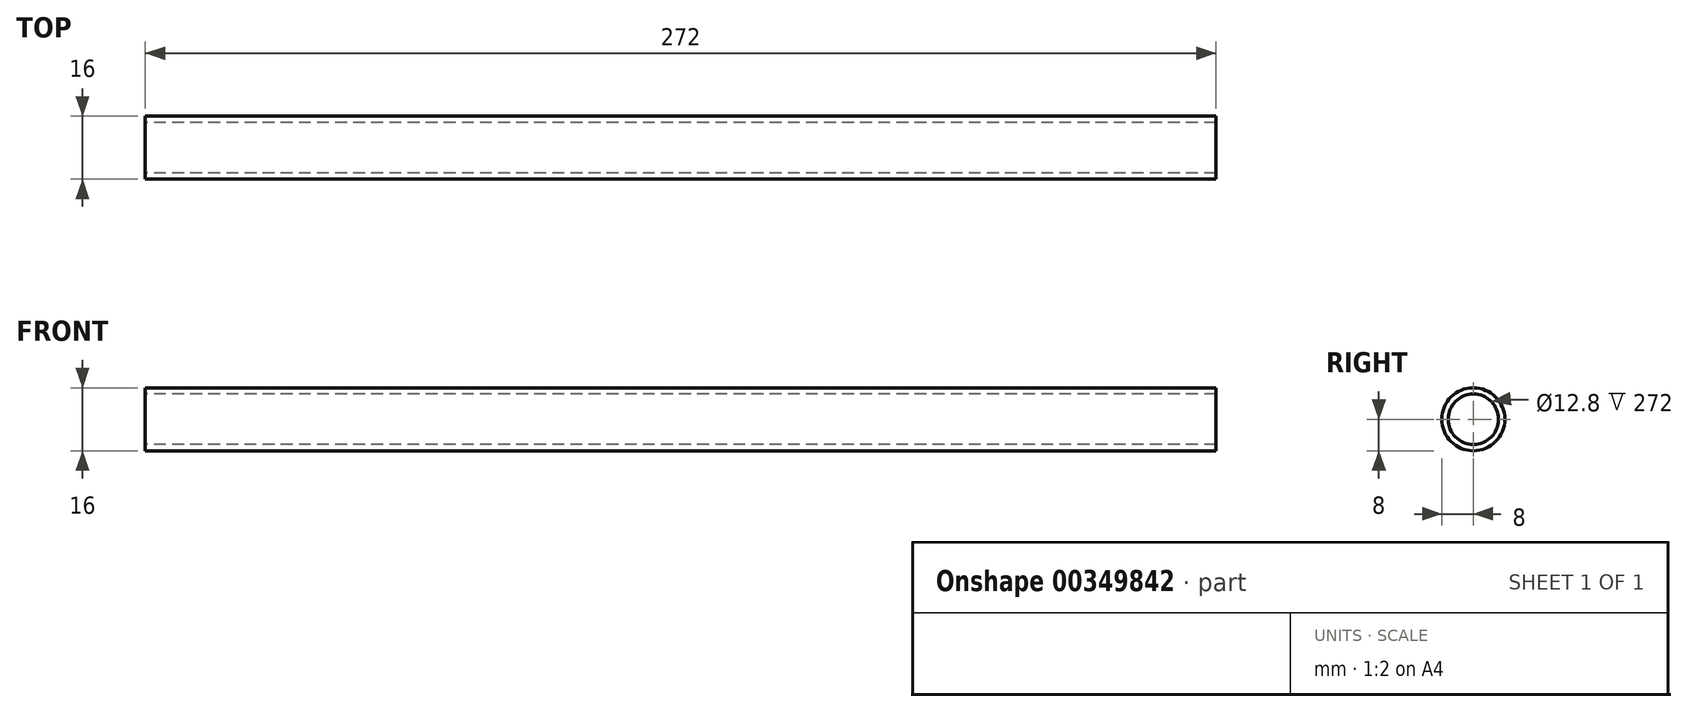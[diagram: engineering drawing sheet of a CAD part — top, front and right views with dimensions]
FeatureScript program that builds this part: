
annotation { "Feature Type Name" : "Feature", "Feature Type Description" : "" }
export const myFeature = defineFeature(function(context is Context, id is Id, definition is map)
    precondition{}
    {
        {
            var Q0;
            Q0=qCreatedBy(makeId("Right.planeOp"),FACE);
            var sketch = newSketch(context, id + "F0", { "sketchPlane" : qUnion([Q0])});
            skCircle(sketch, "E0", {"center": v(0, 0) * mm, "radius": 8 * mm});
            skCircle(sketch, "E1", {"center": v(0, 0) * mm, "radius": 6.4 * mm});
            skSolve(sketch);
        }
        {
            var Q0;
            Q0 = qSketchRegion(id + "F0", true);
            extrude(context, id + "F1", {"entities" : qUnion([Q0]), "depth" : 136 * mm, "hasSecondDirection" : true, "secondDirectionOppositeDirection" : true, "secondDirectionDepth" : 136 * mm});
        }
    });
